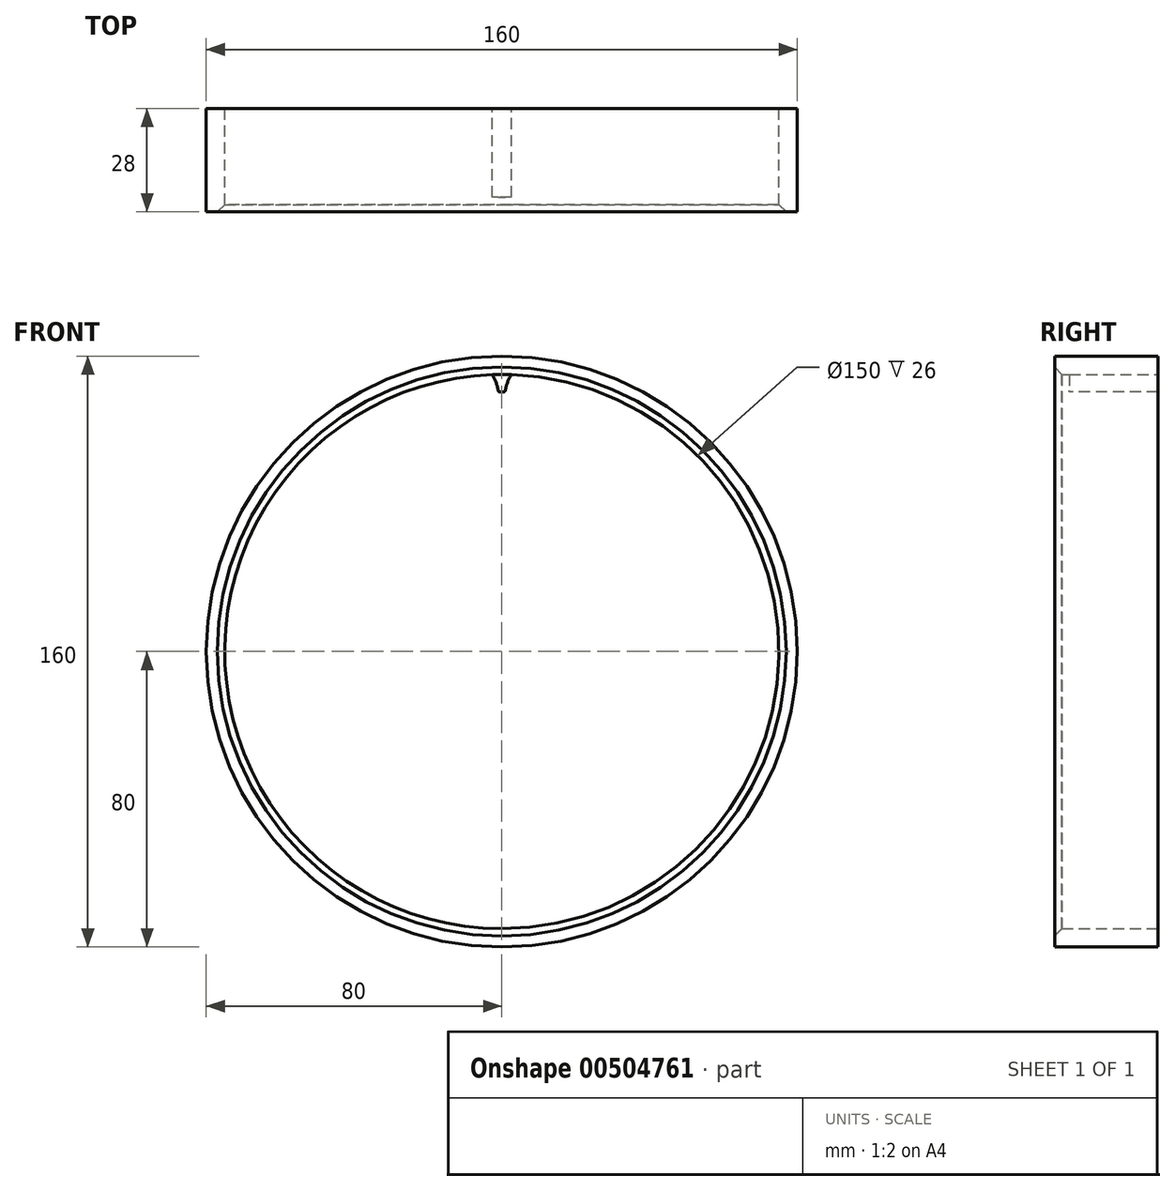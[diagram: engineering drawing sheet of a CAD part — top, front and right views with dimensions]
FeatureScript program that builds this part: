
annotation { "Feature Type Name" : "Feature", "Feature Type Description" : "" }
export const myFeature = defineFeature(function(context is Context, id is Id, definition is map)
    precondition{}
    {
        {
            var Q0;
            Q0=qCreatedBy(makeId("Front.planeOp"),FACE);
            var sketch = newSketch(context, id + "F0", { "sketchPlane" : qUnion([Q0])});
            skCircle(sketch, "E0", {"center": v(0, 0) * mm, "radius": 80 * mm});
            skCircle(sketch, "E1", {"center": v(0, 0) * mm, "radius": 75 * mm});
            skSolve(sketch);
        }
        {
            var Q0;
            Q0 = qSketchRegion(id + "F0", true);
            extrude(context, id + "F1", {"entities" : qUnion([Q0]), "depth" : 28 * mm, "offsetDistance" : 25 * mm, "symmetric" : true});
        }
        {
            var Q0;
            Q0=qCreatedBy(makeId("Front.planeOp"),FACE);
            var sketch = newSketch(context, id + "F2", { "sketchPlane" : qUnion([Q0])});
            skLineSegment(sketch, "E2", {"start": v(0, 0) * mm, "end": v(0, 75) * mm, "construction": true});
            skArc(sketch, "E3", {"start": v(2.62, 74.95) * mm, "mid": v(0, 75) * mm, "end": v(-2.63, 74.95) * mm});
            skLineSegment(sketch, "E4", {"start": v(-0.9, 70.24) * mm, "end": v(0.9, 70.24) * mm});
            skCircle(sketch, "E5", {"center": v(0, 0) * mm, "radius": 70.25 * mm, "construction": true});
            skArc(sketch, "E6", {"start": v(-0.9, 70.24) * mm, "mid": v(-1.5, 72.7) * mm, "end": v(-2.62, 74.95) * mm});
            skArc(sketch, "E7", {"start": v(2.63, 74.95) * mm, "mid": v(1.5, 72.7) * mm, "end": v(0.9, 70.24) * mm});
            skLineSegment(sketch, "E8", {"start": v(-2.62, 74.95) * mm, "end": v(2.62, 74.95) * mm, "construction": true});
            skSolve(sketch);
        }
        {
            var Q0;
            Q0 = qSketchRegion(id + "F2", true);
            var Q1;
            Q1=makeQuery(id+"F1.opExtrude","CAP_FACE",FACE,{"disambiguationData":[OSD([sQuery(id+"F0.wireOp",EDGE,"E0"),sQuery(id+"F0.wireOp",EDGE,"E1")])],"isStart":false});
            var Q2;
            Q2=makeQuery(id+"F1.opExtrude","CAP_FACE",FACE,{"disambiguationData":[OSD([sQuery(id+"F0.wireOp",EDGE,"E0"),sQuery(id+"F0.wireOp",EDGE,"E1")])],"isStart":true});
            extrude(context, id + "F3", {"entities" : qUnion([Q0]), "operationType" : NewBodyOperationType.ADD, "depth" : 10 * mm, "endBoundEntityFace" : qUnion([Q1]), "offsetDistance" : 25 * mm, "hasSecondDirection" : true, "secondDirectionBound" : BoundingType.UP_TO_SURFACE, "secondDirectionOppositeDirection" : true, "secondDirectionDepth" : 25 * mm, "secondDirectionBoundEntityFace" : qUnion([Q2])});
        }
        {
            var Q0;
            Q0=makeQuery(id+"F3.opExtrude","SWEPT_EDGE",EDGE,{"disambiguationData":[OSD([sQuery(id+"F2.wireOp",EDGE,"E3"),sQuery(id+"F2.wireOp",EDGE,"E6")])]});
            var Q1;
            Q1=makeQuery(id+"F3.opExtrude","SWEPT_EDGE",EDGE,{"disambiguationData":[OSD([sQuery(id+"F2.wireOp",EDGE,"E4"),sQuery(id+"F2.wireOp",EDGE,"E6")])]});
            var Q2;
            Q2=makeQuery(id+"F3.opExtrude","SWEPT_EDGE",EDGE,{"disambiguationData":[OSD([sQuery(id+"F2.wireOp",EDGE,"E4"),sQuery(id+"F2.wireOp",EDGE,"E7")])]});
            var Q3;
            Q3=makeQuery(id+"F3.opExtrude","SWEPT_EDGE",EDGE,{"disambiguationData":[OSD([sQuery(id+"F2.wireOp",EDGE,"E3"),sQuery(id+"F2.wireOp",EDGE,"E7")])]});
            fillet(context, id + "F4", {"entities" : qUnion([Q0, Q1, Q2, Q3]), "radius" : 0.5 * mm, "tangentPropagation" : true, "allowEdgeOverflow" : false});
        }
        {
            var Q0;
            Q0=makeQuery(id+"F1.opExtrude","CAP_EDGE",EDGE,{"disambiguationData":[OSD([sQuery(id+"F0.wireOp",EDGE,"E1")])],"isStart":false});
            chamfer(context, id + "F5", {"entities" : qUnion([Q0]), "width" : 2 * mm, "tangentPropagation" : true});
        }
    });
